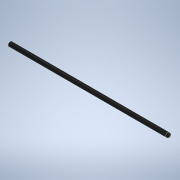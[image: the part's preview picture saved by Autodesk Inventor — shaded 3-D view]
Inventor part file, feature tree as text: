
AUTODESK INVENTOR PART (.ipt)
format: ipt  version: 2022 (Build 260153000, 153)  size: 96,768 bytes
history: native  units: in
note: dims shown in document units (in); Inventor stores cm internally (conversion verified against a paired STEP export)
features: extrude x1, fillet x1, sketch x1
ambient origin geometry x8: Origin, YZ Plane, XZ Plane, XY Plane, X Axis, Y Axis, Z Axis, Center Point
bodies: Solid1 (feature_tree)
feature tree (3):
  extrude  "Extrusion1"  Depth=1.0in TaperAngle=0.0deg
  fillet  "Fillet1"  Radius=0.0125in
  sketch  "Sketch1"  dims[d0=0.0275in d1=1.0in d2=0.0in d3=0.0125in]
